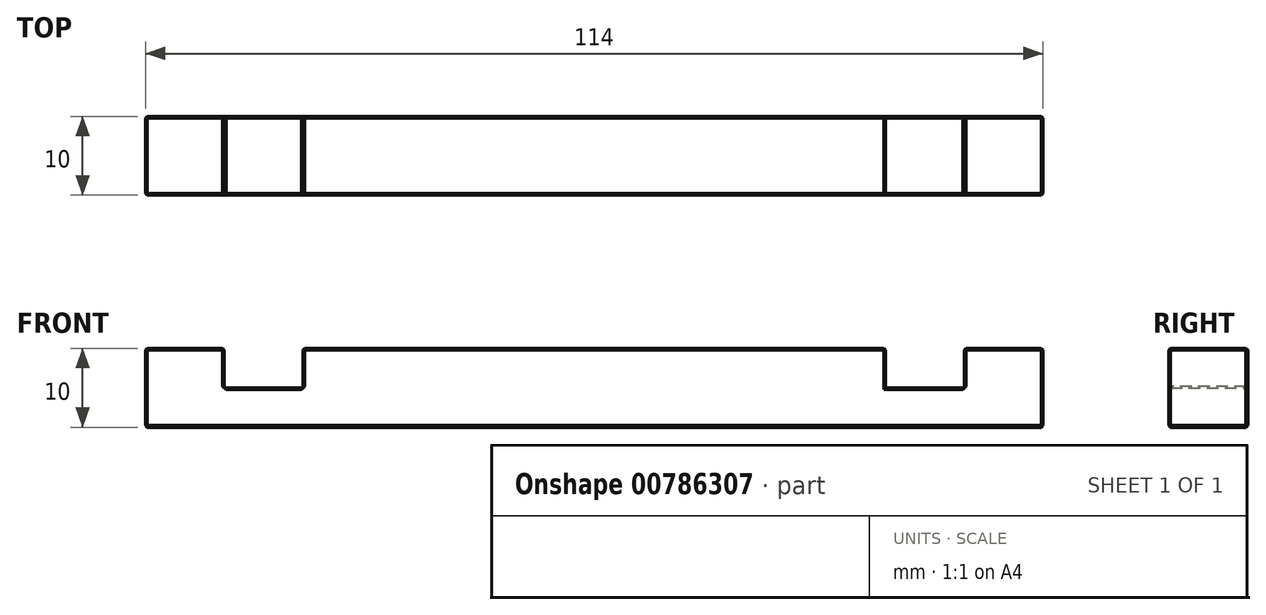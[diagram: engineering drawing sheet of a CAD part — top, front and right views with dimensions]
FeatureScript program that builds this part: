
annotation { "Feature Type Name" : "Feature", "Feature Type Description" : "" }
export const myFeature = defineFeature(function(context is Context, id is Id, definition is map)
    precondition{}
    {
        {
            var Q0;
            Q0=qCreatedBy(makeId("Front.planeOp"),FACE);
            var sketch = newSketch(context, id + "F0", { "sketchPlane" : qUnion([Q0])});
            skLineSegment(sketch, "E0", {"start": v(-55.39, 10) * mm, "end": v(-55.39, 0) * mm});
            skLineSegment(sketch, "E1", {"start": v(-55.39, 0) * mm, "end": v(58.61, 0) * mm});
            skLineSegment(sketch, "E2", {"start": v(58.61, 10) * mm, "end": v(48.61, 10) * mm});
            skLineSegment(sketch, "E3", {"start": v(48.61, 10) * mm, "end": v(48.61, 5) * mm});
            skLineSegment(sketch, "E4", {"start": v(48.61, 5) * mm, "end": v(38.61, 5) * mm});
            skLineSegment(sketch, "E5", {"start": v(38.61, 5) * mm, "end": v(38.61, 10) * mm});
            skLineSegment(sketch, "E6", {"start": v(38.61, 10) * mm, "end": v(-35.39, 10) * mm});
            skLineSegment(sketch, "E7", {"start": v(-35.39, 10) * mm, "end": v(-35.39, 5) * mm});
            skLineSegment(sketch, "E8", {"start": v(-35.39, 5) * mm, "end": v(-45.39, 5) * mm});
            skLineSegment(sketch, "E9", {"start": v(-45.39, 5) * mm, "end": v(-45.39, 10) * mm});
            skLineSegment(sketch, "E10", {"start": v(-45.39, 10) * mm, "end": v(-55.39, 10) * mm});
            skLineSegment(sketch, "E11", {"start": v(58.61, 10) * mm, "end": v(58.61, 0) * mm});
            skSolve(sketch);
        }
        {
            var Q0;
            Q0=makeQuery(id+"F0.imprint","IMPRINT",FACE,{"disambiguationData":[TD([[makeQuery(id+"F0.imprint","IMPRINT",EDGE,{"derivedFrom":sQuery(id+"F0.wireOp",EDGE,"E0")}),1.0]])]});
            extrude(context, id + "F1", {"entities" : qUnion([Q0]), "depth" : 10 * mm, "offsetDistance" : 25 * mm});
        }
        {
            var Q0;
            Q0=makeQuery(id+"F1.opExtrude","CAP_FACE",FACE,{"disambiguationData":[OSD([sQuery(id+"F0.wireOp",EDGE,"E0"),sQuery(id+"F0.wireOp",EDGE,"E1"),sQuery(id+"F0.wireOp",EDGE,"E2"),sQuery(id+"F0.wireOp",EDGE,"E3"),sQuery(id+"F0.wireOp",EDGE,"E4"),sQuery(id+"F0.wireOp",EDGE,"E5"),sQuery(id+"F0.wireOp",EDGE,"E6"),sQuery(id+"F0.wireOp",EDGE,"E7"),sQuery(id+"F0.wireOp",EDGE,"E8"),sQuery(id+"F0.wireOp",EDGE,"E9"),sQuery(id+"F0.wireOp",EDGE,"E10"),sQuery(id+"F0.wireOp",EDGE,"E11")])],"isStart":false});
            var Q1;
            Q1=makeQuery(id+"F1.opExtrude","SWEPT_FACE",FACE,{"disambiguationData":[OSD([sQuery(id+"F0.wireOp",EDGE,"E6")])]});
            var Q2;
            Q2=makeQuery(id+"F1.opExtrude","SWEPT_FACE",FACE,{"disambiguationData":[OSD([sQuery(id+"F0.wireOp",EDGE,"E8")])]});
            var Q3;
            Q3=makeQuery(id+"F1.opExtrude","SWEPT_FACE",FACE,{"disambiguationData":[OSD([sQuery(id+"F0.wireOp",EDGE,"E10")])]});
            var Q4;
            Q4=makeQuery(id+"F1.opExtrude","CAP_FACE",FACE,{"disambiguationData":[OSD([sQuery(id+"F0.wireOp",EDGE,"E0"),sQuery(id+"F0.wireOp",EDGE,"E1"),sQuery(id+"F0.wireOp",EDGE,"E2"),sQuery(id+"F0.wireOp",EDGE,"E3"),sQuery(id+"F0.wireOp",EDGE,"E4"),sQuery(id+"F0.wireOp",EDGE,"E5"),sQuery(id+"F0.wireOp",EDGE,"E6"),sQuery(id+"F0.wireOp",EDGE,"E7"),sQuery(id+"F0.wireOp",EDGE,"E8"),sQuery(id+"F0.wireOp",EDGE,"E9"),sQuery(id+"F0.wireOp",EDGE,"E10"),sQuery(id+"F0.wireOp",EDGE,"E11")])],"isStart":true});
            var Q5;
            Q5=makeQuery(id+"F1.opExtrude","SWEPT_FACE",FACE,{"disambiguationData":[OSD([sQuery(id+"F0.wireOp",EDGE,"E11")])]});
            var Q6;
            Q6=makeQuery(id+"F1.opExtrude","CAP_EDGE",EDGE,{"disambiguationData":[OSD([sQuery(id+"F0.wireOp",EDGE,"E4")])],"isStart":true});
            var Q7;
            Q7=makeQuery(id+"F1.opExtrude","SWEPT_FACE",FACE,{"disambiguationData":[OSD([sQuery(id+"F0.wireOp",EDGE,"E3")])]});
            var Q8;
            Q8=makeQuery(id+"F1.opExtrude","SWEPT_FACE",FACE,{"disambiguationData":[OSD([sQuery(id+"F0.wireOp",EDGE,"E0")])]});
            chamfer(context, id + "F2", {"entities" : qUnion([Q0, Q1, Q2, Q3, Q4, Q5, Q6, Q7, Q8]), "width" : 0.2 * mm, "tangentPropagation" : true});
        }
    });
